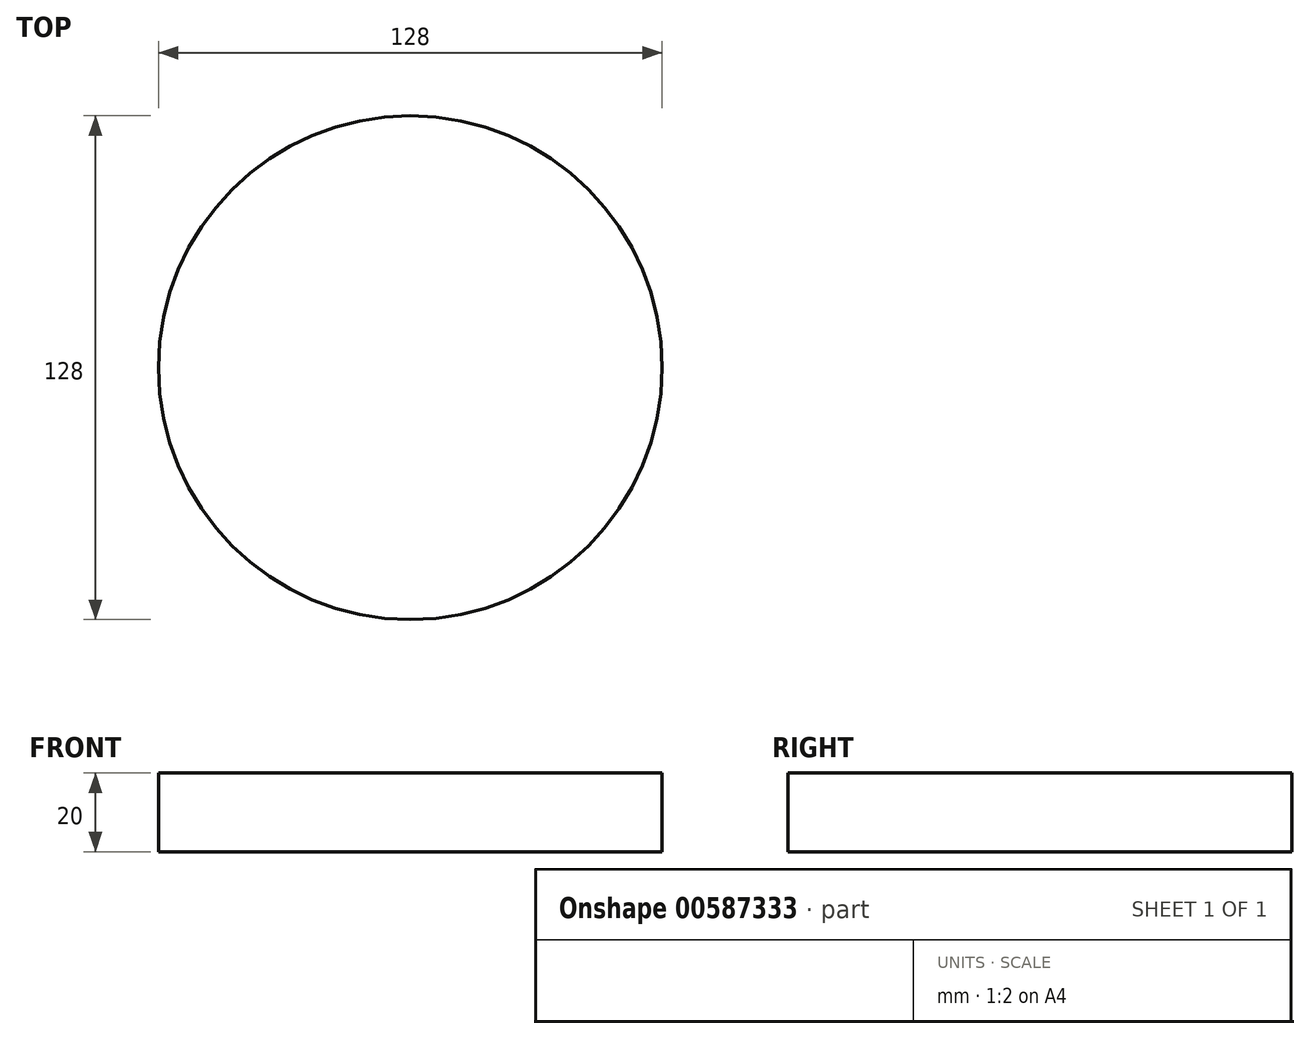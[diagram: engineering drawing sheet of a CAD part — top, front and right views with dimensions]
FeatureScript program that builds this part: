
annotation { "Feature Type Name" : "Feature", "Feature Type Description" : "" }
export const myFeature = defineFeature(function(context is Context, id is Id, definition is map)
    precondition{}
    {
        {
            var Q0;
            Q0=qCreatedBy(makeId("Top.planeOp"),FACE);
            var sketch = newSketch(context, id + "F0", { "sketchPlane" : qUnion([Q0])});
            skCircle(sketch, "E0", {"center": v(0, 0) * mm, "radius": 64 * mm});
            skSolve(sketch);
        }
        {
            var Q0;
            Q0 = qSketchRegion(id + "F0", true);
            extrude(context, id + "F1", {"entities" : qUnion([Q0]), "depth" : 20 * mm, "offsetDistance" : 25 * mm});
        }
    });
